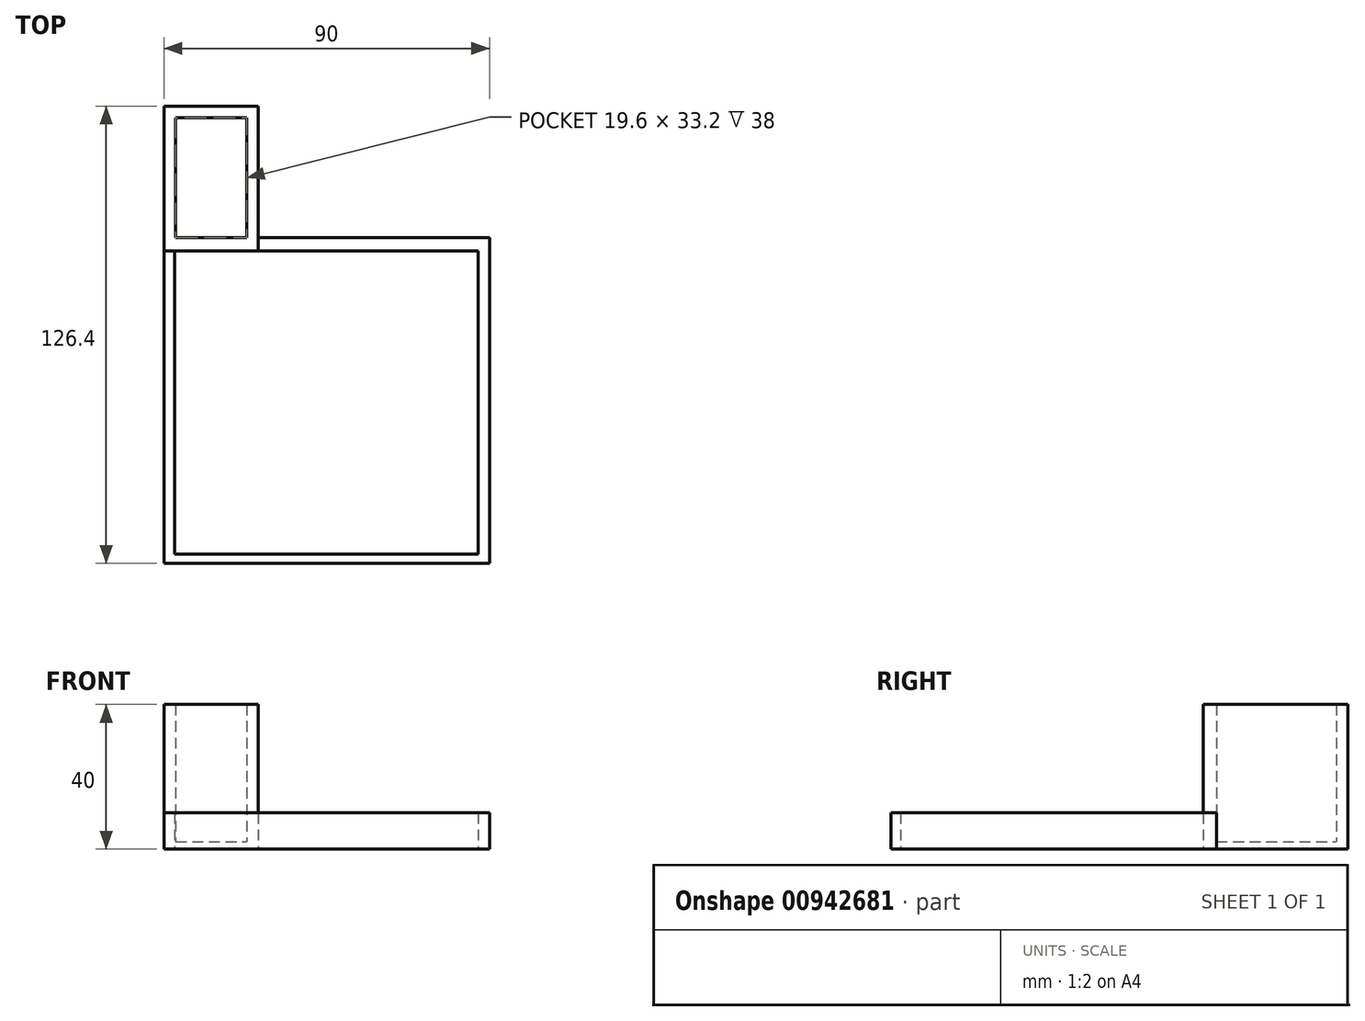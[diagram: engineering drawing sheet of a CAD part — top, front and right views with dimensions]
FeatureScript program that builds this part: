
annotation { "Feature Type Name" : "Feature", "Feature Type Description" : "" }
export const myFeature = defineFeature(function(context is Context, id is Id, definition is map)
    precondition{}
    {
        {
            var Q0;
            Q0=qCreatedBy(makeId("Top.planeOp"),FACE);
            var sketch = newSketch(context, id + "F0", { "sketchPlane" : qUnion([Q0])});
            skLineSegment(sketch, "E0.bottom", {"start": v(90, -90) * mm, "end": v(0, -90) * mm});
            skLineSegment(sketch, "E0.top", {"start": v(90, 0) * mm, "end": v(26, 0) * mm});
            skLineSegment(sketch, "E0.left", {"start": v(90, -90) * mm, "end": v(90, 0) * mm});
            skLineSegment(sketch, "E0.right", {"start": v(0, -90) * mm, "end": v(0, 0) * mm});
            skLineSegment(sketch, "E1.bottom", {"start": v(90, -90) * mm, "end": v(86.8, -90) * mm});
            skLineSegment(sketch, "E1.left", {"start": v(90, -90) * mm, "end": v(90, -87.4) * mm});
            skLineSegment(sketch, "E2.top", {"start": v(0, -3.6) * mm, "end": v(2.9, -3.6) * mm});
            skLineSegment(sketch, "E2.left", {"start": v(0, 0) * mm, "end": v(0, -3.6) * mm});
            skLineSegment(sketch, "E3.bottom", {"start": v(2.9, -3.6) * mm, "end": v(86.8, -3.6) * mm});
            skLineSegment(sketch, "E3.top", {"start": v(2.9, -87.4) * mm, "end": v(86.8, -87.4) * mm});
            skLineSegment(sketch, "E3.left", {"start": v(2.9, -3.6) * mm, "end": v(2.9, -87.4) * mm});
            skLineSegment(sketch, "E3.right", {"start": v(86.8, -3.6) * mm, "end": v(86.8, -87.4) * mm});
            skLineSegment(sketch, "E4.bottom", {"start": v(0, -3.6) * mm, "end": v(26, -3.6) * mm});
            skLineSegment(sketch, "E4.top", {"start": v(0, 36.4) * mm, "end": v(26, 36.4) * mm});
            skLineSegment(sketch, "E4.left", {"start": v(0, -3.6) * mm, "end": v(0, 36.4) * mm});
            skLineSegment(sketch, "E4.right", {"start": v(26, -3.6) * mm, "end": v(26, 36.4) * mm});
            skLineSegment(sketch, "E5.0", {"start": v(3.2, 33.2) * mm, "end": v(22.8, 33.2) * mm});
            skLineSegment(sketch, "E6.0", {"start": v(22.8, 0) * mm, "end": v(22.8, 33.2) * mm});
            skLineSegment(sketch, "E7.0", {"start": v(3.2, 0) * mm, "end": v(3.2, 33.2) * mm});
            skLineSegment(sketch, "E8.trimOffspring", {"start": v(22.8, 0) * mm, "end": v(3.2, 0) * mm});
            skSolve(sketch);
        }
        {
            var Q0;
            {var subQ14=sQuery(id+"F0.wireOp",EDGE,"E8.trimOffspring");Q0=makeQuery(id+"F0.imprint","IMPRINT",FACE,{"disambiguationData":[TD([[makeQuery(id+"F0.imprint","IMPRINT",EDGE,{"derivedFrom":subQ14}),1.0]])]});}
            var Q1;
            {var subQ0=sQuery(id+"F0.wireOp",EDGE,"E6.0");var subQ1=sQuery(id+"F0.wireOp",EDGE,"E4.top");var subQ2=makeQuery(id+"F0.imprint","INTERSECT",VERTEX,{"derivedFrom":[subQ1,subQ0]});Q1=makeQuery(id+"F0.imprint","IMPRINT",FACE,{"disambiguationData":[TD([[makeQuery(id+"F0.imprint","IMPRINT",EDGE,{"disambiguationData":[TD([[subQ2,1.0]])],"derivedFrom":subQ1}),-1.0]])]});}
            var Q2;
            {var subQ0=sQuery(id+"F0.wireOp",EDGE,"E4.right");var subQ1=sQuery(id+"F0.wireOp",EDGE,"E4.top");var subQ2=makeQuery(id+"F0.imprint","INTERSECT",VERTEX,{"derivedFrom":[subQ1,subQ0]});Q2=makeQuery(id+"F0.imprint","IMPRINT",FACE,{"disambiguationData":[TD([[makeQuery(id+"F0.imprint","IMPRINT",EDGE,{"disambiguationData":[TD([[subQ2,1.0]])],"derivedFrom":subQ1}),-1.0]])]});}
            var Q3;
            {var subQ0=sQuery(id+"F0.wireOp",EDGE,"E4.left");var subQ1=sQuery(id+"F0.wireOp",EDGE,"E4.top");var subQ2=makeQuery(id+"F0.imprint","INTERSECT",VERTEX,{"derivedFrom":[subQ1,subQ0]});Q3=makeQuery(id+"F0.imprint","IMPRINT",FACE,{"disambiguationData":[TD([[makeQuery(id+"F0.imprint","IMPRINT",EDGE,{"disambiguationData":[TD([[subQ2,-1.0]])],"derivedFrom":subQ1}),-1.0]])]});}
            extrude(context, id + "F1", {"entities" : qUnion([Q0, Q1, Q2, Q3]), "depth" : 40 * mm, "offsetDistance" : 25 * mm});
        }
        {
            var Q0;
            Q0=makeQuery(id+"F0.imprint","IMPRINT",FACE,{"disambiguationData":[TD([[makeQuery(id+"F0.imprint","IMPRINT",EDGE,{"derivedFrom":sQuery(id+"F0.wireOp",EDGE,"E0.bottom")}),-1.0]])]});
            extrude(context, id + "F2", {"entities" : qUnion([Q0]), "operationType" : NewBodyOperationType.ADD, "depth" : 10 * mm, "offsetDistance" : 25 * mm});
        }
        {
            var Q0;
            {var subQ5=sQuery(id+"F0.wireOp",EDGE,"E8.trimOffspring");Q0=makeQuery(id+"F0.imprint","IMPRINT",FACE,{"disambiguationData":[TD([[makeQuery(id+"F0.imprint","IMPRINT",EDGE,{"derivedFrom":subQ5}),-1.0]])]});}
            extrude(context, id + "F3", {"entities" : qUnion([Q0]), "operationType" : NewBodyOperationType.ADD, "depth" : 2 * mm, "offsetDistance" : 25 * mm});
        }
    });
